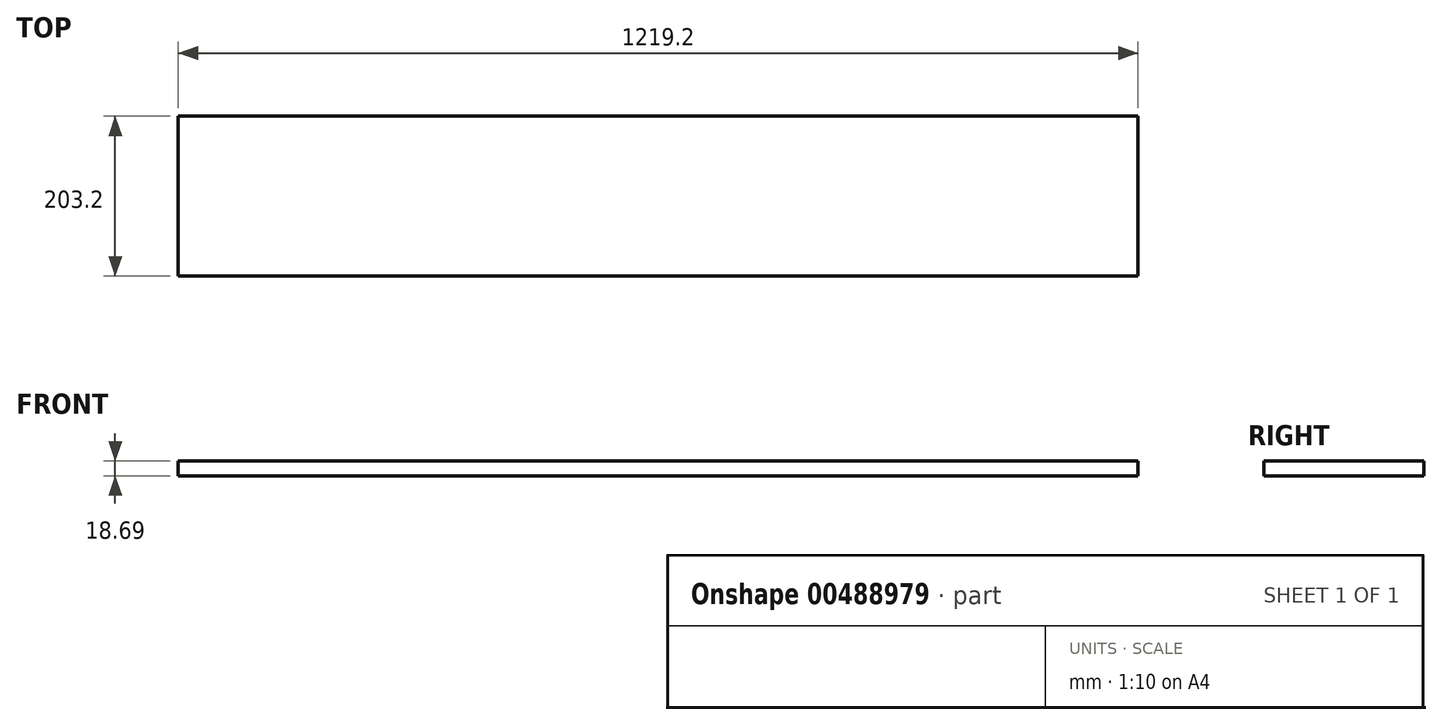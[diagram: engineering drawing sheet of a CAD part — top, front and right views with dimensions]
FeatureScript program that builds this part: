
annotation { "Feature Type Name" : "Feature", "Feature Type Description" : "" }
export const myFeature = defineFeature(function(context is Context, id is Id, definition is map)
    precondition{}
    {
        {
            var Q0;
            Q0=qCreatedBy(makeId("Top.planeOp"),FACE);
            var sketch = newSketch(context, id + "F0", { "sketchPlane" : qUnion([Q0])});
            skLineSegment(sketch, "E0.bottom", {"start": v(-100.3, 176) * mm, "end": v(1118.9, 176) * mm});
            skLineSegment(sketch, "E0.top", {"start": v(-100.3, -27.2) * mm, "end": v(1118.9, -27.2) * mm});
            skLineSegment(sketch, "E0.left", {"start": v(-100.3, 176) * mm, "end": v(-100.3, -27.2) * mm});
            skLineSegment(sketch, "E0.right", {"start": v(1118.9, 176) * mm, "end": v(1118.9, -27.2) * mm});
            skSolve(sketch);
        }
        {
            var Q0;
            Q0=makeQuery(id+"F0.imprint","IMPRINT",FACE,{"disambiguationData":[TD([[makeQuery(id+"F0.imprint","IMPRINT",EDGE,{"derivedFrom":sQuery(id+"F0.wireOp",EDGE,"E0.bottom")}),-1.0]])]});
            extrude(context, id + "F1", {"entities" : qUnion([Q0]), "depth" : 18.7 * mm, "offsetDistance" : 25.4 * mm});
        }
    });
